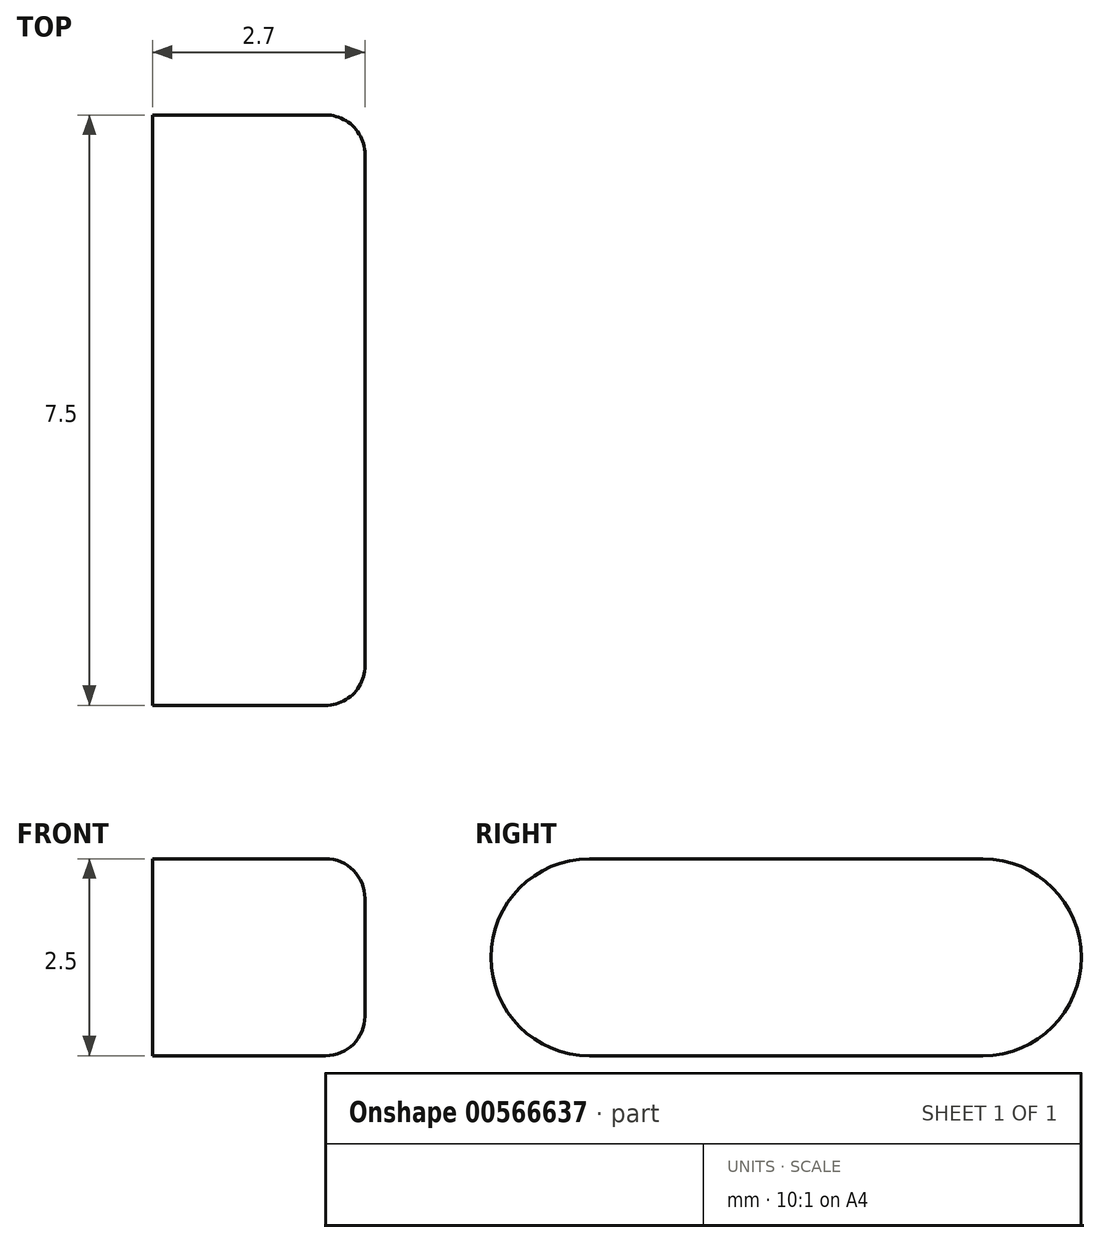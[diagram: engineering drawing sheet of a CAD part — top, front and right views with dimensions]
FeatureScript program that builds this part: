
annotation { "Feature Type Name" : "Feature", "Feature Type Description" : "" }
export const myFeature = defineFeature(function(context is Context, id is Id, definition is map)
    precondition{}
    {
        {
            var Q0;
            Q0=qCreatedBy(makeId("Right.planeOp"),FACE);
            var sketch = newSketch(context, id + "F0", { "sketchPlane" : qUnion([Q0])});
            skLineSegment(sketch, "E0.bottom", {"start": v(-2.5, 1.25) * mm, "end": v(2.5, 1.25) * mm});
            skLineSegment(sketch, "E0.top", {"start": v(-2.5, -1.25) * mm, "end": v(2.5, -1.25) * mm});
            skPoint(sketch, "E0.middle", {"position": v(0, 0) * mm});
            skArc(sketch, "E1", {"start": v(2.5, -1.25) * mm, "mid": v(3.75, 0) * mm, "end": v(2.5, 1.25) * mm});
            skArc(sketch, "E2", {"start": v(-2.5, 1.25) * mm, "mid": v(-3.75, 0) * mm, "end": v(-2.5, -1.25) * mm});
            skSolve(sketch);
        }
        {
            var Q0;
            Q0=qSketchRegion(id+"F0",true);
            extrude(context, id + "F1", {"entities" : qUnion([Q0]), "endBound" : BoundingType.SYMMETRIC, "depth" : 2.7 * mm, "offsetDistance" : 25 * mm});
        }
        {
            var Q0;
            Q0=makeQuery(id+"F1.opExtrude","CAP_FACE",FACE,{"disambiguationData":[OSD([sQuery(id+"F0.wireOp",EDGE,"E0.bottom"),sQuery(id+"F0.wireOp",EDGE,"E0.top"),sQuery(id+"F0.wireOp",EDGE,"E1"),sQuery(id+"F0.wireOp",EDGE,"E2")])],"isStart":false});
            fillet(context, id + "F2", {"entities" : qUnion([Q0]), "radius" : 0.5 * mm, "tangentPropagation" : true, "allowEdgeOverflow" : false});
        }
    });
